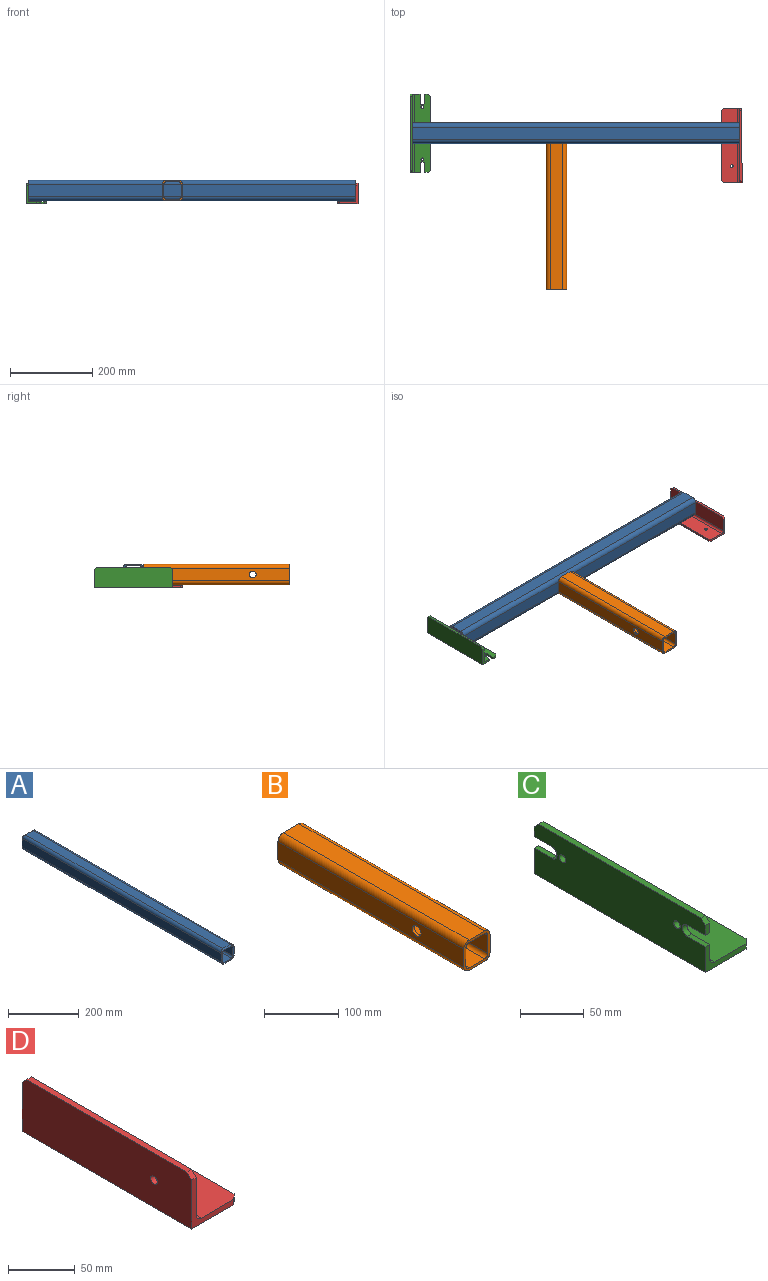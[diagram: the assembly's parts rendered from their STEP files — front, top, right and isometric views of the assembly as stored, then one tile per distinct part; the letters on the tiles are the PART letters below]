
ASSEMBLY  parts=4 mates=3
PART A: 20 faces, bbox 50x795x50 mm
  f0: plane 795x30mm, normal (1,0,0), area 23850mm2, adj f4,f5,f6,f9
  f1: plane 785x30mm, normal (0,0,1), area 23550mm2, adj f6,f7,f18,f19
  f2: plane 795x30mm, normal (-1,0,0), area 23850mm2, adj f4,f5,f7,f8
  f3: plane 795x30mm, normal (0,0,-1), area 23850mm2, adj f4,f5,f8,f9
  f4: plane 50x45mm, normal (0,-1,0), area 504.1mm2, adj f0,f2,f3,f6,f7,f8,f9,f10
  f5: plane 50x45mm, normal (0,1,0), area 504.1mm2, adj f0,f2,f3,f6,f7,f8,f9,f10
  f6: cylinder r=10mm len=795mm, axis (0,-1,0), area 12419.3mm2, adj f0,f1,f4,f5,f18,f19
  f7: cylinder r=10mm len=795mm, axis (0,1,0), area 12419.3mm2, adj f1,f2,f4,f5,f18,f19
  f8: cylinder r=10mm len=795mm, axis (0,-1,0), area 12487.8mm2, adj f2,f3,f4,f5
  f9: cylinder r=10mm len=795mm, axis (0,1,0), area 12487.8mm2, adj f0,f3,f4,f5
  f10: plane 795x30mm, normal (-1,0,0), area 23850mm2, adj f4,f5,f11,f17
  f11: cylinder r=6mm len=795mm, axis (0,-1,0), area 7488mm2, adj f4,f5,f10,f12,f18,f19
  f12: plane 793x30mm, normal (0,0,-1), area 23790mm2, adj f11,f13,f18,f19
  f13: cylinder r=6mm len=795mm, axis (0,-1,0), area 7488mm2, adj f4,f5,f12,f14,f18,f19
  f14: plane 795x30mm, normal (1,0,0), area 23850mm2, adj f4,f5,f13,f15
  f15: cylinder r=6mm len=795mm, axis (0,-1,0), area 7492.7mm2, adj f4,f5,f14,f16
  f16: plane 795x30mm, normal (0,0,1), area 23850mm2, adj f4,f5,f15,f17
  f17: cylinder r=6mm len=795mm, axis (0,-1,0), area 7492.7mm2, adj f4,f5,f10,f16
  f18: plane 47.32x5mm, normal (0,-0.71,0.71), area 250.2mm2, adj f1,f4,f6,f7,f11,f12,f13
  f19: plane 47.32x5mm, normal (0,0.71,0.71), area 250.2mm2, adj f1,f5,f6,f7,f11,f12,f13
PART B: 20 faces, bbox 50x355x50 mm
  f0: plane 355x30mm, normal (1,0,0), area 10436.2mm2, adj f4,f5,f6,f9,f19
  f1: plane 355x30mm, normal (0,0,1), area 10650mm2, adj f4,f5,f6,f7
  f2: plane 355x30mm, normal (-1,0,0), area 10436.2mm2, adj f4,f5,f7,f8,f18
  f3: plane 355x30mm, normal (0,0,-1), area 10650mm2, adj f4,f5,f8,f9
  f4: plane 50x50mm, normal (0,-1,0), area 681.1mm2, adj f0,f1,f2,f3,f6,f7,f8,f9
  f5: plane 50x50mm, normal (0,1,0), area 681.1mm2, adj f0,f1,f2,f3,f6,f7,f8,f9
  f6: cylinder r=10mm len=355mm, axis (0,-1,0), area 5576.3mm2, adj f0,f1,f4,f5
  f7: cylinder r=10mm len=355mm, axis (0,1,0), area 5576.3mm2, adj f1,f2,f4,f5
  f8: cylinder r=10mm len=355mm, axis (0,-1,0), area 5576.3mm2, adj f2,f3,f4,f5
  f9: cylinder r=10mm len=355mm, axis (0,1,0), area 5576.3mm2, adj f0,f3,f4,f5
  f10: plane 355x30mm, normal (-1,0,0), area 10436.2mm2, adj f4,f5,f11,f17,f19
  f11: cylinder r=6mm len=355mm, axis (0,-1,0), area 3345.8mm2, adj f4,f5,f10,f12
  f12: plane 355x30mm, normal (0,0,-1), area 10650mm2, adj f4,f5,f11,f13
  f13: cylinder r=6mm len=355mm, axis (0,-1,0), area 3345.8mm2, adj f4,f5,f12,f14
  f14: plane 355x30mm, normal (1,0,0), area 10436.2mm2, adj f4,f5,f13,f15,f18
  f15: cylinder r=6mm len=355mm, axis (0,-1,0), area 3345.8mm2, adj f4,f5,f14,f16
  f16: plane 355x30mm, normal (0,0,1), area 10650mm2, adj f4,f5,f15,f17
  f17: cylinder r=6mm len=355mm, axis (0,-1,0), area 3345.8mm2, adj f4,f5,f10,f16
  f18: cylinder r=8.25mm len=16.5mm, axis (-1,0,0), area 207.3mm2, adj f2,f14
  f19: cylinder r=8.25mm len=16.5mm, axis (-1,0,0), area 207.3mm2, adj f0,f10
PART C: 23 faces, bbox 50x190x50 mm
  f0: plane 190x50mm, normal (-1,0,0), area 8863mm2, adj f2,f3,f4,f7,f8,f9,f11,f12
  f1: plane 190x40mm, normal (1,0,0), area 6963mm2, adj f2,f3,f7,f8,f9,f10,f11,f12
  f2: plane 45x24.5mm, normal (0,-1,0), area 327.9mm2, adj f0,f1,f4,f6,f10,f13,f21
  f3: plane 9.5x5mm, normal (0,1,0), area 47.5mm2, adj f0,f1,f11,f17
  f4: plane 190x50mm, normal (0,0,-1), area 9475mm2, adj f0,f2,f5,f9,f13,f14
  f5: plane 180x5mm, normal (1,0,0), area 900mm2, adj f4,f6,f13,f14
  f6: plane 190x40mm, normal (0,0,1), area 7575mm2, adj f2,f5,f9,f10,f13,f14
  f7: plane 180x5mm, normal (0,0,1), area 900mm2, adj f0,f1,f11,f12
  f8: plane 9.5x5mm, normal (0,-1,0), area 47.5mm2, adj f0,f1,f12,f19
  f9: plane 45x24.5mm, normal (0,1,0), area 327.9mm2, adj f0,f1,f4,f6,f10,f14,f15
  f10: cylinder r=5mm len=190mm, axis (0,-1,0), area 1492.3mm2, adj f1,f2,f6,f9
  f11: plane 5x5mm, normal (0,0.71,0.71), area 35.4mm2, adj f0,f1,f3,f7
  f12: plane 5x5mm, normal (0,-0.71,0.71), area 35.4mm2, adj f0,f1,f7,f8
  f13: plane 5x5mm, normal (0.71,-0.71,0), area 35.4mm2, adj f2,f4,f5,f6
  f14: plane 5x5mm, normal (0.71,0.71,0), area 35.4mm2, adj f4,f5,f6,f9
  f15: plane 20x5mm, normal (0,0,1), area 100mm2, adj f0,f1,f9,f16
  f16: cylinder r=5.5mm len=11mm, axis (-1,0,0), area 86.4mm2, adj f0,f1,f15,f17
  f17: plane 20x5mm, normal (0,0,-1), area 100mm2, adj f0,f1,f3,f16
  f18: cylinder r=3.5mm len=7mm, axis (-1,0,0), area 110mm2, adj f0,f1
  f19: plane 20x5mm, normal (0,0,-1), area 100mm2, adj f0,f1,f8,f20
  f20: cylinder r=5.5mm len=11mm, axis (-1,0,0), area 86.4mm2, adj f0,f1,f19,f21
  f21: plane 20x5mm, normal (0,0,1), area 100mm2, adj f0,f1,f2,f20
  f22: cylinder r=3.5mm len=7mm, axis (-1,0,0), area 110mm2, adj f0,f1
PART D: 14 faces, bbox 50x180x50 mm
  f0: plane 180x50mm, normal (-1,0,0), area 8936.5mm2, adj f1,f5,f6,f7,f9,f10,f13
  f1: plane 180x50mm, normal (0,0,-1), area 8975mm2, adj f0,f2,f6,f7,f11,f12
  f2: plane 170x5mm, normal (1,0,0), area 850mm2, adj f1,f3,f11,f12
  f3: plane 180x40mm, normal (0,0,1), area 7175mm2, adj f2,f6,f7,f8,f11,f12
  f4: plane 180x40mm, normal (1,0,0), area 7136.5mm2, adj f5,f6,f7,f8,f9,f10,f13
  f5: plane 170x5mm, normal (0,0,1), area 850mm2, adj f0,f4,f9,f10
  f6: plane 45x45mm, normal (0,-1,0), area 430.4mm2, adj f0,f1,f3,f4,f8,f10,f11
  f7: plane 45x45mm, normal (0,1,0), area 430.4mm2, adj f0,f1,f3,f4,f8,f9,f12
  f8: cylinder r=5mm len=180mm, axis (0,-1,0), area 1413.7mm2, adj f3,f4,f6,f7
  f9: plane 5x5mm, normal (0,0.71,0.71), area 35.4mm2, adj f0,f4,f5,f7
  f10: plane 5x5mm, normal (0,-0.71,0.71), area 35.4mm2, adj f0,f4,f5,f6
  f11: plane 5x5mm, normal (0.71,-0.71,0), area 35.4mm2, adj f1,f2,f3,f6
  f12: plane 5x5mm, normal (0.71,0.71,0), area 35.4mm2, adj f1,f2,f3,f7
  f13: cylinder r=3.5mm len=7mm, axis (-1,0,0), area 110mm2, adj f0,f4
PLACE A rot(axis=(0.71,0.71,0),180deg) t=(47.5,25,0)mm
PLACE B at identity fixed
PLACE C rot(axis=(0.71,0,0.71),180deg) t=(-355,25,-31.96)mm
PLACE D rot(axis=(0,-1,0),90deg) t=(450,85,-31.96)mm
MATE fastened C.f6 <-> A.f4  axis (1,0,0) through (-350,25,-2.02)mm
MATE fastened D.f3 <-> A.f5  axis (-1,0,0) through (445,-5,-2.02)mm
MATE fastened B.f5 <-> A.f2  axis (0,1,0) through (0,0,0)mm
